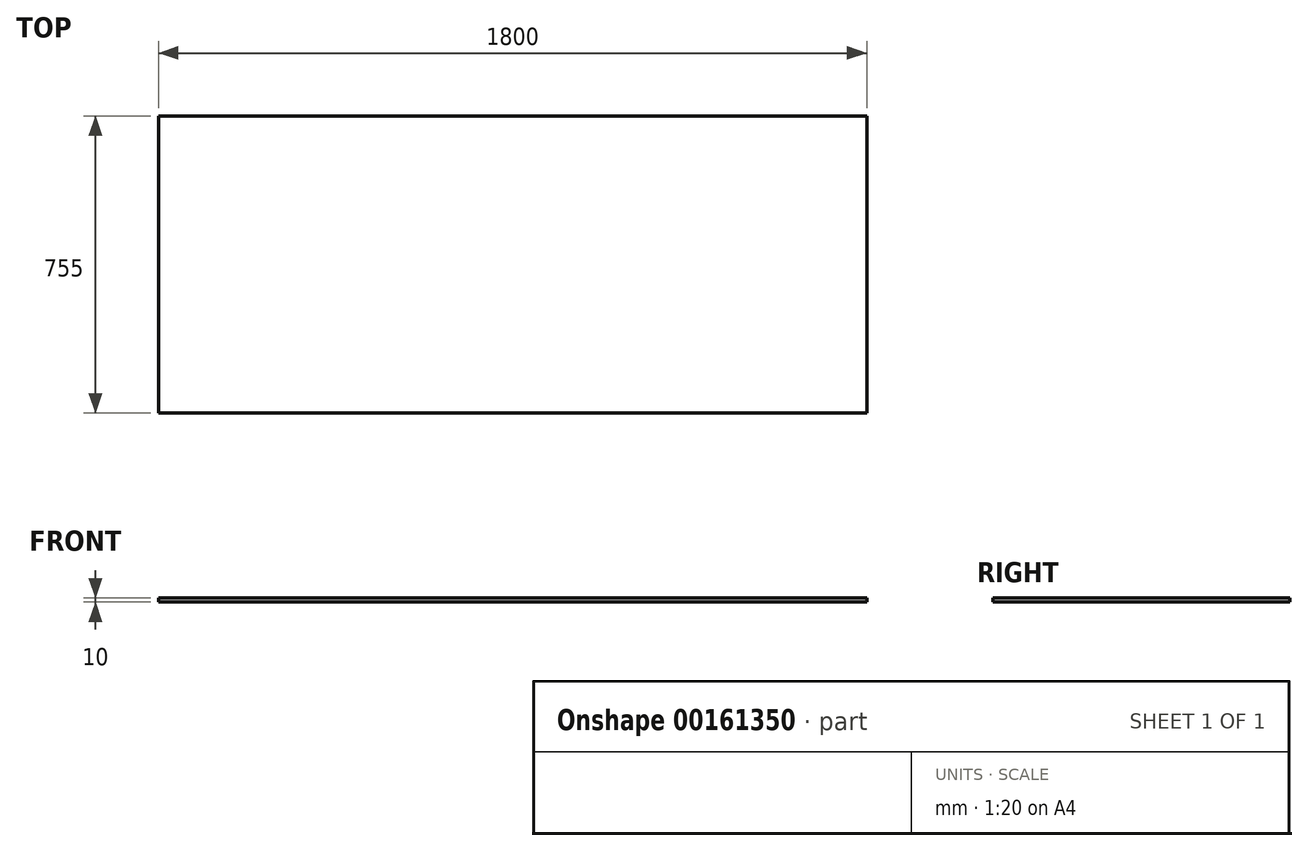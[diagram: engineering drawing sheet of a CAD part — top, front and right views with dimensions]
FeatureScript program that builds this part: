
annotation { "Feature Type Name" : "Feature", "Feature Type Description" : "" }
export const myFeature = defineFeature(function(context is Context, id is Id, definition is map)
    precondition{}
    {
        {
            var Q0;
            Q0=qCreatedBy(makeId("Top.planeOp"),FACE);
            var sketch = newSketch(context, id + "F0", { "sketchPlane" : qUnion([Q0])});
            skLineSegment(sketch, "E0.bottom", {"start": v(900, -377.5) * mm, "end": v(-900, -377.5) * mm});
            skLineSegment(sketch, "E0.top", {"start": v(900, 377.5) * mm, "end": v(-900, 377.5) * mm});
            skLineSegment(sketch, "E0.left", {"start": v(900, -377.5) * mm, "end": v(900, 377.5) * mm});
            skLineSegment(sketch, "E0.right", {"start": v(-900, -377.5) * mm, "end": v(-900, 377.5) * mm});
            skPoint(sketch, "E0.middle", {"position": v(0, 0) * mm});
            skSolve(sketch);
        }
        {
            var Q0;
            Q0=makeQuery(id+"F0.imprint","IMPRINT",FACE,{"disambiguationData":[TD([[makeQuery(id+"F0.imprint","IMPRINT",EDGE,{"derivedFrom":sQuery(id+"F0.wireOp",EDGE,"E0.bottom")}),-1.0]])]});
            extrude(context, id + "F1", {"entities" : qUnion([Q0]), "depth" : 10 * mm});
        }
    });
